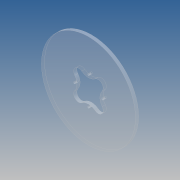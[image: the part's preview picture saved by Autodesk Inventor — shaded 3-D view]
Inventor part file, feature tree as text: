
AUTODESK INVENTOR PART (.ipt)
format: ipt  version: 2017 (Build 210142000, 142)  size: 135,168 bytes
history: native  units: mm
features: reference x5, other x4, extrude x1, sketch x1
ambient origin geometry x8: Origin, YZ Plane, XZ Plane, XY Plane, X Axis, Y Axis, Z Axis, Center Point
bodies: Body1 (feature_tree)
feature tree (11):
  other  "Sólido1"
  extrude  "Extrusión1"  Depth=5.0mm
  sketch  "Boceto1"  dims[d0=30.0mm d1=150.0mm d2=5.0mm d3=0.0mm]
  reference  "Referencia1"
  reference  "Referencia2"
  reference  "Referencia3"
  reference  "Referencia4"
  reference  "Referencia5"
  other  "<userpath>\Dropbox\E\Caja Motriz\transmision Engranajes\Plato Carrete.iam"
  other  "Plato Carrete.iam"
  other  "carrete:1"
